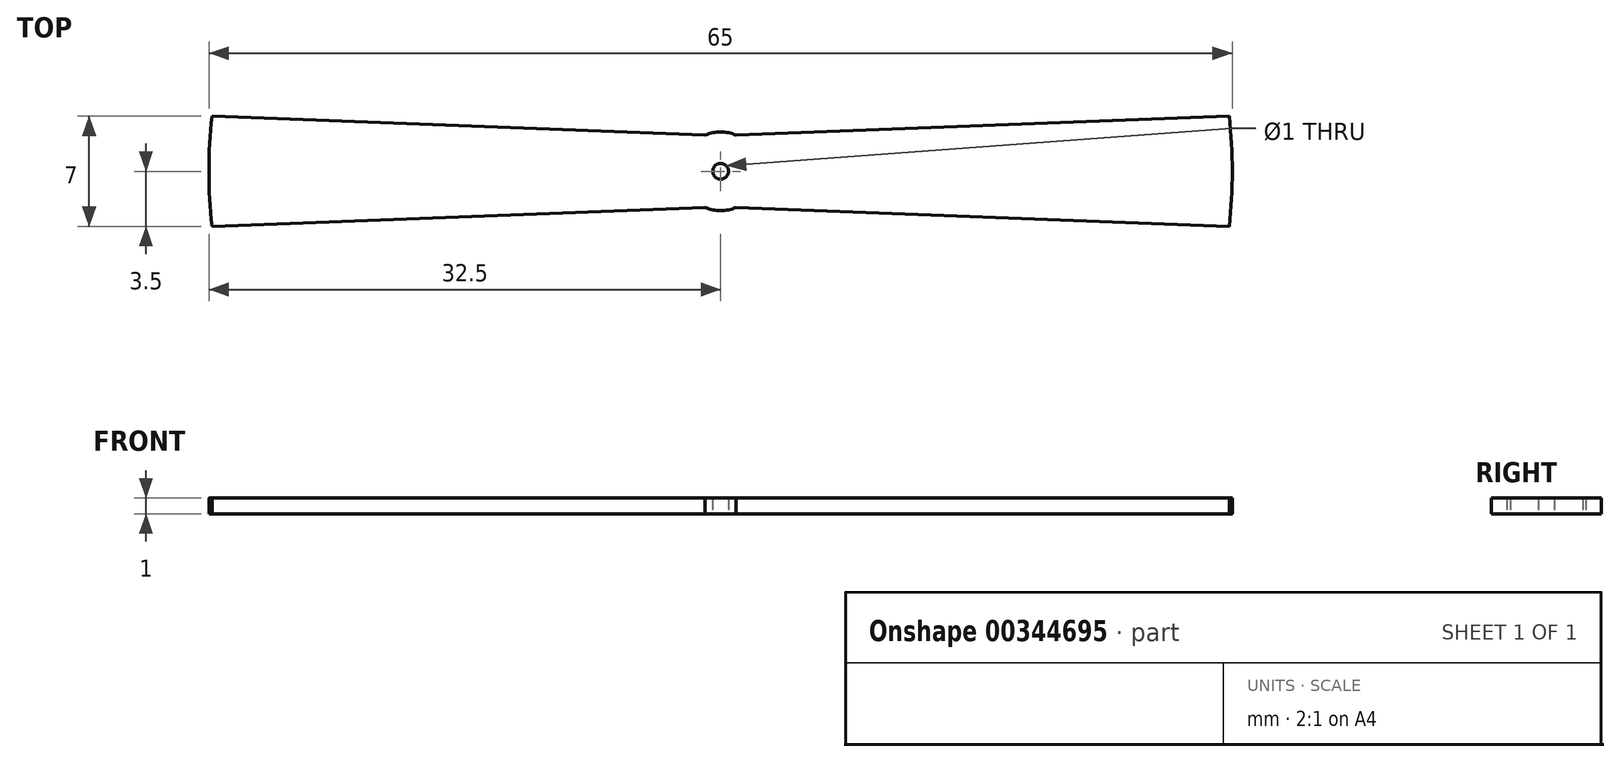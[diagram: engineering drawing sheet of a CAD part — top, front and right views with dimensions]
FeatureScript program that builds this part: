
annotation { "Feature Type Name" : "Feature", "Feature Type Description" : "" }
export const myFeature = defineFeature(function(context is Context, id is Id, definition is map)
    precondition{}
    {
        {
            var Q0;
            Q0=qCreatedBy(makeId("Top.planeOp"),FACE);
            var sketch = newSketch(context, id + "F0", { "sketchPlane" : qUnion([Q0])});
            skArc(sketch, "E0", {"start": v(-0.98, -2.3) * mm, "mid": v(0, -2.5) * mm, "end": v(0.98, -2.3) * mm});
            skCircle(sketch, "E1", {"center": v(0, 0) * mm, "radius": 0.5 * mm});
            skLineSegment(sketch, "E2", {"start": v(-0.98, 2.3) * mm, "end": v(-32.31, 3.5) * mm});
            skArc(sketch, "E3", {"start": v(-32.31, 3.5) * mm, "mid": v(-32.5, 0) * mm, "end": v(-32.31, -3.5) * mm});
            skLineSegment(sketch, "E4.MirrorCS", {"start": v(-0.98, -2.3) * mm, "end": v(-32.31, -3.5) * mm});
            skLineSegment(sketch, "E5.MirrorCS", {"start": v(0.98, 2.3) * mm, "end": v(32.31, 3.5) * mm});
            skLineSegment(sketch, "E6.MirrorCS", {"start": v(0.98, -2.3) * mm, "end": v(32.31, -3.5) * mm});
            skArc(sketch, "E7.trimOffspring", {"start": v(0.98, 2.3) * mm, "mid": v(0, 2.5) * mm, "end": v(-0.98, 2.3) * mm});
            skArc(sketch, "E8.trimOffspring", {"start": v(32.31, -3.5) * mm, "mid": v(32.5, 0) * mm, "end": v(32.31, 3.5) * mm});
            skSolve(sketch);
        }
        {
            var Q0;
            Q0=makeQuery(id+"F0.imprint","IMPRINT",FACE,{"disambiguationData":[TD([[makeQuery(id+"F0.imprint","IMPRINT",EDGE,{"derivedFrom":sQuery(id+"F0.wireOp",EDGE,"E0")}),1.0]])]});
            extrude(context, id + "F1", {"entities" : qUnion([Q0]), "depth" : 1 * mm});
        }
    });
